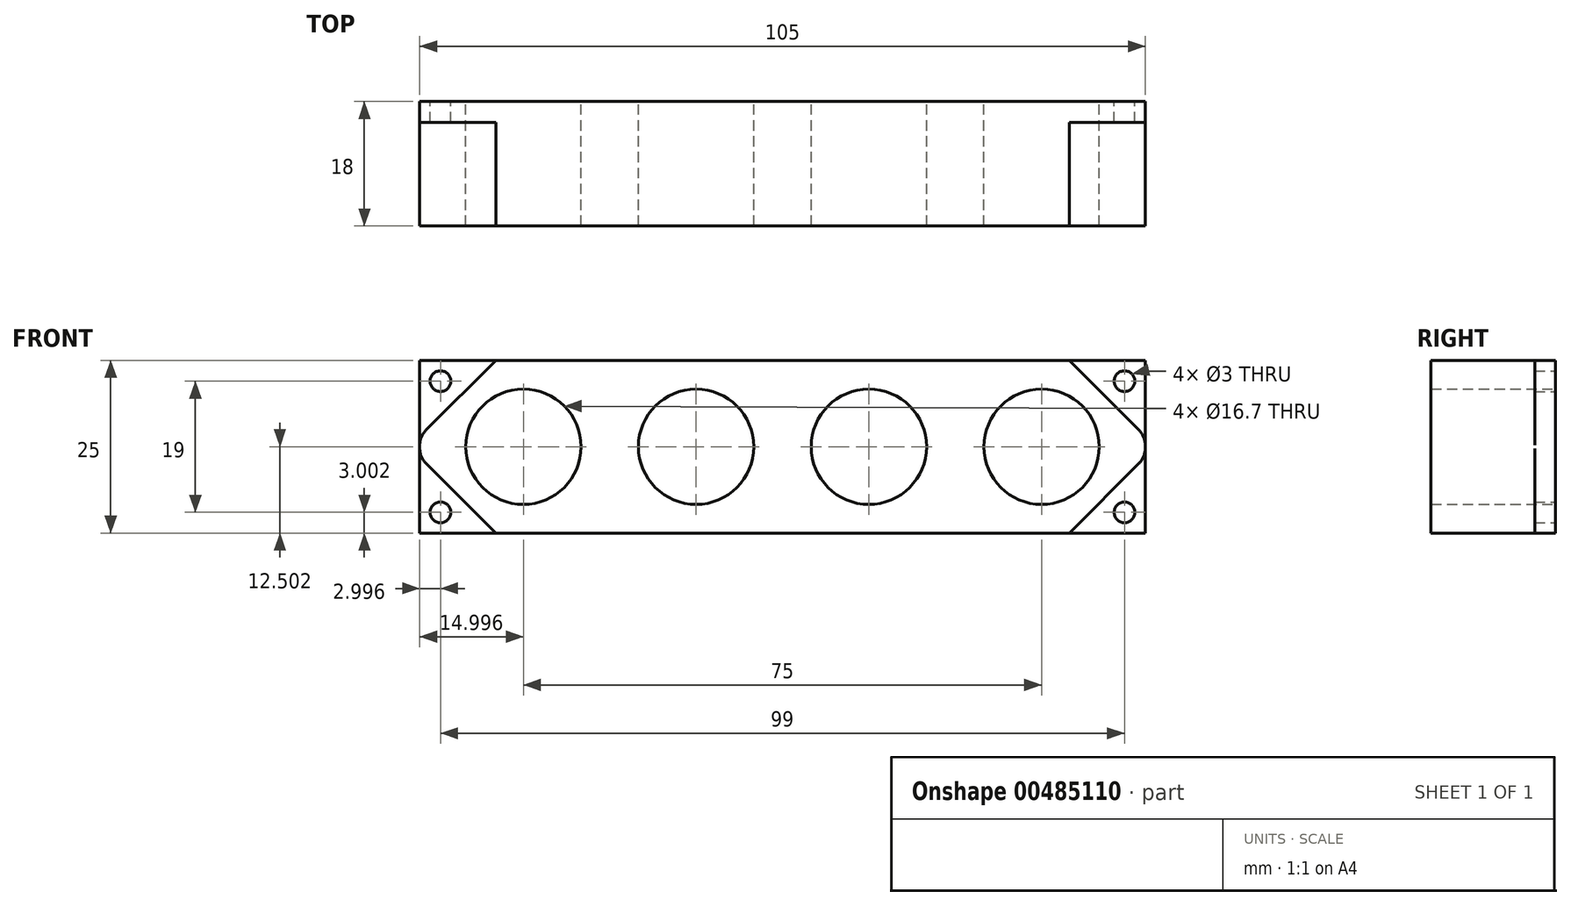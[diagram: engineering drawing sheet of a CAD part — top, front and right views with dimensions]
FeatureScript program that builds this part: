
annotation { "Feature Type Name" : "Feature", "Feature Type Description" : "" }
export const myFeature = defineFeature(function(context is Context, id is Id, definition is map)
    precondition{}
    {
        {
            var Q0;
            Q0=qCreatedBy(makeId("Front.planeOp"),FACE);
            var sketch = newSketch(context, id + "F0", { "sketchPlane" : qUnion([Q0])});
            skLineSegment(sketch, "E0.bottom", {"start": v(-48.3, 6.84) * mm, "end": v(56.7, 6.84) * mm, "construction": true});
            skLineSegment(sketch, "E0.top", {"start": v(-48.3, -5.66) * mm, "end": v(56.7, -5.66) * mm});
            skLineSegment(sketch, "E0.left", {"start": v(-48.3, 6.84) * mm, "end": v(-48.3, -5.66) * mm});
            skLineSegment(sketch, "E0.right", {"start": v(56.7, 6.84) * mm, "end": v(56.7, -5.66) * mm});
            skLineSegment(sketch, "E1", {"start": v(-33.3, 6.84) * mm, "end": v(-33.3, -5.66) * mm, "construction": true});
            skLineSegment(sketch, "E2", {"start": v(-8.3, 6.84) * mm, "end": v(-8.3, -5.66) * mm, "construction": true});
            skLineSegment(sketch, "E3", {"start": v(16.7, 6.84) * mm, "end": v(16.7, -5.66) * mm, "construction": true});
            skCircle(sketch, "E4", {"center": v(-33.3, 6.84) * mm, "radius": 8.35 * mm});
            skCircle(sketch, "E5", {"center": v(-8.3, 6.84) * mm, "radius": 8.35 * mm});
            skCircle(sketch, "E6", {"center": v(16.7, 6.84) * mm, "radius": 8.35 * mm});
            skLineSegment(sketch, "E7", {"start": v(41.7, 6.84) * mm, "end": v(41.7, -5.66) * mm, "construction": true});
            skCircle(sketch, "E8", {"center": v(41.7, 6.84) * mm, "radius": 8.35 * mm});
            skLineSegment(sketch, "E9.top", {"start": v(-48.3, 19.34) * mm, "end": v(56.7, 19.34) * mm});
            skLineSegment(sketch, "E9.left", {"start": v(-48.3, 6.84) * mm, "end": v(-48.3, 19.34) * mm});
            skLineSegment(sketch, "E9.right", {"start": v(56.7, 6.84) * mm, "end": v(56.7, 19.34) * mm});
            skLineSegment(sketch, "E10", {"start": v(-45.3, 19.34) * mm, "end": v(-45.3, -5.66) * mm, "construction": true});
            skLineSegment(sketch, "E11", {"start": v(53.7, 19.34) * mm, "end": v(53.7, -5.66) * mm, "construction": true});
            skLineSegment(sketch, "E12", {"start": v(-48.3, -2.66) * mm, "end": v(56.7, -2.66) * mm, "construction": true});
            skLineSegment(sketch, "E13", {"start": v(-48.3, 16.34) * mm, "end": v(56.7, 16.34) * mm, "construction": true});
            skCircle(sketch, "E14", {"center": v(-45.3, 16.34) * mm, "radius": 1.5 * mm});
            skCircle(sketch, "E15", {"center": v(-45.3, -2.66) * mm, "radius": 1.5 * mm});
            skCircle(sketch, "E16", {"center": v(53.7, 16.34) * mm, "radius": 1.5 * mm});
            skCircle(sketch, "E17", {"center": v(53.7, -2.66) * mm, "radius": 1.5 * mm});
            skLineSegment(sketch, "E18", {"start": v(-48.3, 8.34) * mm, "end": v(56.7, 8.34) * mm, "construction": true});
            skLineSegment(sketch, "E19", {"start": v(-48.3, 5.34) * mm, "end": v(56.7, 5.34) * mm, "construction": true});
            skLineSegment(sketch, "E20", {"start": v(45.7, 19.34) * mm, "end": v(45.7, -5.66) * mm, "construction": true});
            skLineSegment(sketch, "E21", {"start": v(-37.3, 19.34) * mm, "end": v(-37.3, -5.66) * mm, "construction": true});
            skLineSegment(sketch, "E22", {"start": v(45.7, 19.34) * mm, "end": v(56.7, 8.34) * mm});
            skLineSegment(sketch, "E23", {"start": v(56.7, 5.34) * mm, "end": v(45.7, -5.66) * mm});
            skLineSegment(sketch, "E24", {"start": v(-48.3, 5.34) * mm, "end": v(-37.3, -5.66) * mm});
            skLineSegment(sketch, "E25", {"start": v(-48.3, 8.34) * mm, "end": v(-37.3, 19.34) * mm});
            skSolve(sketch);
        }
        {
            var Q0;
            Q0=makeQuery(id+"F0.imprint","IMPRINT",FACE,{"disambiguationData":[TD([[makeQuery(id+"F0.imprint","IMPRINT",EDGE,{"derivedFrom":sQuery(id+"F0.wireOp",EDGE,"E14")}),-1.0]])]});
            var Q1;
            Q1=makeQuery(id+"F0.imprint","IMPRINT",FACE,{"disambiguationData":[TD([[makeQuery(id+"F0.imprint","IMPRINT",EDGE,{"derivedFrom":sQuery(id+"F0.wireOp",EDGE,"E15")}),-1.0]])]});
            var Q2;
            Q2=makeQuery(id+"F0.imprint","IMPRINT",FACE,{"disambiguationData":[TD([[makeQuery(id+"F0.imprint","IMPRINT",EDGE,{"derivedFrom":sQuery(id+"F0.wireOp",EDGE,"E4")}),-1.0]])]});
            var Q3;
            Q3=makeQuery(id+"F0.imprint","IMPRINT",FACE,{"disambiguationData":[TD([[makeQuery(id+"F0.imprint","IMPRINT",EDGE,{"derivedFrom":sQuery(id+"F0.wireOp",EDGE,"E16")}),-1.0]])]});
            var Q4;
            Q4=makeQuery(id+"F0.imprint","IMPRINT",FACE,{"disambiguationData":[TD([[makeQuery(id+"F0.imprint","IMPRINT",EDGE,{"derivedFrom":sQuery(id+"F0.wireOp",EDGE,"E17")}),-1.0]])]});
            extrude(context, id + "F1", {"entities" : qUnion([Q0, Q1, Q2, Q3, Q4]), "depth" : 3 * mm, "offsetDistance" : 25 * mm});
        }
        {
            var Q0;
            Q0=makeQuery(id+"F0.imprint","IMPRINT",FACE,{"disambiguationData":[TD([[makeQuery(id+"F0.imprint","IMPRINT",EDGE,{"derivedFrom":sQuery(id+"F0.wireOp",EDGE,"E4")}),-1.0]])]});
            extrude(context, id + "F2", {"entities" : qUnion([Q0]), "operationType" : NewBodyOperationType.ADD, "depth" : 18 * mm, "offsetDistance" : 25 * mm});
        }
        {
            var Q0;
            Q0=makeQuery(id+"F2.opExtrude","SWEPT_EDGE",EDGE,{"disambiguationData":[OSD([sQuery(id+"F0.wireOp",EDGE,"E9.left"),sQuery(id+"F0.wireOp",EDGE,"E25")])]});
            var Q1;
            Q1=makeQuery(id+"F2.opExtrude","SWEPT_EDGE",EDGE,{"disambiguationData":[OSD([sQuery(id+"F0.wireOp",EDGE,"E0.left"),sQuery(id+"F0.wireOp",EDGE,"E24")])]});
            var Q2;
            Q2=makeQuery(id+"F2.opExtrude","SWEPT_EDGE",EDGE,{"disambiguationData":[OSD([sQuery(id+"F0.wireOp",EDGE,"E0.right"),sQuery(id+"F0.wireOp",EDGE,"E23")])]});
            var Q3;
            Q3=makeQuery(id+"F2.opExtrude","SWEPT_EDGE",EDGE,{"disambiguationData":[OSD([sQuery(id+"F0.wireOp",EDGE,"E9.right"),sQuery(id+"F0.wireOp",EDGE,"E22")])]});
            fillet(context, id + "F3", {"entities" : qUnion([Q0, Q1, Q2, Q3]), "radius" : 3 * mm, "tangentPropagation" : true, "allowEdgeOverflow" : false});
        }
    });
